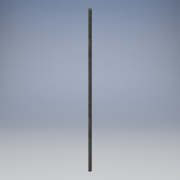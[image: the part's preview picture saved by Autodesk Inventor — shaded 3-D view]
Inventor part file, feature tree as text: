
AUTODESK INVENTOR PART (.ipt)
format: ipt  version: 2016 (Build 200138000, 138)  size: 103,936 bytes
history: native  units: in
note: dims shown in document units (in); Inventor stores cm internally (conversion verified against a paired STEP export)
features: extrude x1, sketch x1
ambient origin geometry x8: Origin, YZ Plane, XZ Plane, XY Plane, X Axis, Y Axis, Z Axis, Center Point
bodies: Solid1 (feature_tree)
feature tree (2):
  extrude  "Extrusion1"  Depth=14.0in TaperAngle=0.0deg
  sketch  "Sketch1"  dims[d0=0.25in d1=14.0in d2=0.0in]
